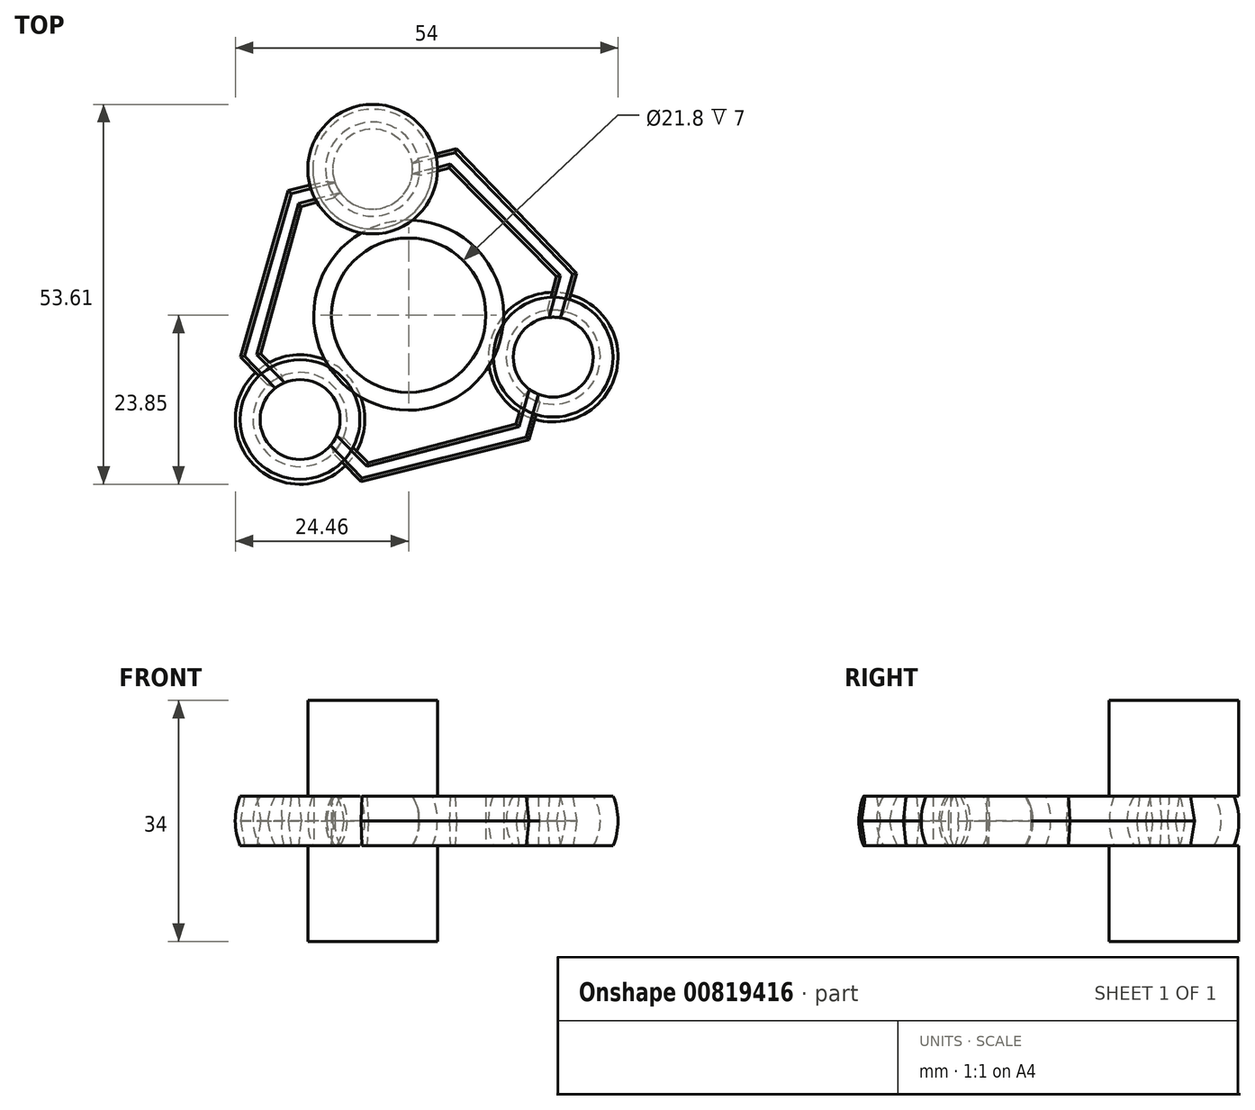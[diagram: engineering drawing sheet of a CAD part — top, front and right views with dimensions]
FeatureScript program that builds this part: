
annotation { "Feature Type Name" : "Feature", "Feature Type Description" : "" }
export const myFeature = defineFeature(function(context is Context, id is Id, definition is map)
    precondition{}
    {
        {
            var Q0;
            Q0=qCreatedBy(makeId("Top.planeOp"),FACE);
            var sketch = newSketch(context, id + "F0", { "sketchPlane" : qUnion([Q0])});
            skCircle(sketch, "E0", {"center": v(0, 0) * mm, "radius": 10.9 * mm});
            skCircle(sketch, "E1", {"center": v(0, 0) * mm, "radius": 13.4 * mm});
            skCircle(sketch, "E2", {"center": v(0, 0) * mm, "radius": 20 * mm, "construction": true});
            skCircle(sketch, "E3", {"center": v(0, 0) * mm, "radius": 18.75 * mm});
            skCircle(sketch, "E4", {"center": v(0, 0) * mm, "radius": 21.25 * mm});
            skSolve(sketch);
        }
        {
            var Q0;
            Q0=makeQuery(id+"F0.imprint","IMPRINT",FACE,{"disambiguationData":[TD([[makeQuery(id+"F0.imprint","IMPRINT",EDGE,{"derivedFrom":sQuery(id+"F0.wireOp",EDGE,"E3")}),-1.0]])]});
            var sketch = newSketch(context, id + "F1", { "sketchPlane" : qUnion([Q0])});
            skCircle(sketch, "E5", {"center": v(-5.08, 20.62) * mm, "radius": 6.64 * mm});
            skCircle(sketch, "E6", {"center": v(-5.08, 20.62) * mm, "radius": 9.14 * mm});
            skSolve(sketch);
        }
        {
            var Q0;
            Q0=makeQuery(id+"F0.imprint","IMPRINT",FACE,{"disambiguationData":[TD([[makeQuery(id+"F0.imprint","IMPRINT",EDGE,{"derivedFrom":sQuery(id+"F0.wireOp",EDGE,"E0")}),1.0]])]});
            var sketch = newSketch(context, id + "F2", { "sketchPlane" : qUnion([Q0])});
            skCircle(sketch, "E7.cCircle", {"center": v(0, 0) * mm, "radius": 21.16 * mm, "construction": true});
            skLineSegment(sketch, "E7.0", {"start": v(-16.97, 17.58) * mm, "end": v(6.74, 23.5) * mm});
            skLineSegment(sketch, "E7.1", {"start": v(6.74, 23.5) * mm, "end": v(23.71, 5.9) * mm});
            skLineSegment(sketch, "E7.2", {"start": v(23.71, 5.9) * mm, "end": v(16.97, -17.58) * mm});
            skLineSegment(sketch, "E7.3", {"start": v(16.97, -17.58) * mm, "end": v(-6.74, -23.5) * mm});
            skLineSegment(sketch, "E7.4", {"start": v(-6.74, -23.5) * mm, "end": v(-23.71, -5.9) * mm});
            skLineSegment(sketch, "E7.5", {"start": v(-23.71, -5.9) * mm, "end": v(-16.97, 17.58) * mm});
            skPoint(sketch, "E7.0.midPoint", {"position": v(-5.12, 20.54) * mm});
            skCircle(sketch, "E8.cCircle", {"center": v(0, 0) * mm, "radius": 18.68 * mm, "construction": true});
            skLineSegment(sketch, "E8.0", {"start": v(-15.15, 15.35) * mm, "end": v(5.72, 20.8) * mm});
            skLineSegment(sketch, "E8.1", {"start": v(5.72, 20.8) * mm, "end": v(20.87, 5.45) * mm});
            skLineSegment(sketch, "E8.2", {"start": v(20.87, 5.45) * mm, "end": v(15.15, -15.35) * mm});
            skLineSegment(sketch, "E8.3", {"start": v(15.15, -15.35) * mm, "end": v(-5.72, -20.8) * mm});
            skLineSegment(sketch, "E8.4", {"start": v(-5.72, -20.8) * mm, "end": v(-20.87, -5.45) * mm});
            skLineSegment(sketch, "E8.5", {"start": v(-20.87, -5.45) * mm, "end": v(-15.15, 15.35) * mm});
            skPoint(sketch, "E8.0.midPoint", {"position": v(-4.72, 18.07) * mm});
            skSolve(sketch);
        }
        {
            var Q0;
            {var subQ0=sQuery(id+"F1.wireOp",EDGE,"E5");var subQ1=makeQuery(id+"F0.imprint","IMPRINT",EDGE,{"derivedFrom":sQuery(id+"F0.wireOp",EDGE,"E4")});var subQ2=makeQuery(id+"F1.imprint","INTERSECT",VERTEX,{"disambiguationData":[OD(0.0)],"derivedFrom":[subQ1,subQ0]});Q0=makeQuery(id+"F1.imprint","IMPRINT",FACE,{"disambiguationData":[TD([[makeQuery(id+"F1.imprint","IMPRINT",EDGE,{"disambiguationData":[TD([[subQ2,1.0]])],"derivedFrom":subQ0}),1.0]])]});}
            var Q1;
            {var subQ0=sQuery(id+"F1.wireOp",EDGE,"E5");var subQ1=makeQuery(id+"F0.imprint","IMPRINT",EDGE,{"derivedFrom":sQuery(id+"F0.wireOp",EDGE,"E4")});var subQ2=makeQuery(id+"F1.imprint","INTERSECT",VERTEX,{"disambiguationData":[OD(0.0)],"derivedFrom":[subQ1,subQ0]});Q1=makeQuery(id+"F1.imprint","IMPRINT",FACE,{"disambiguationData":[TD([[makeQuery(id+"F1.imprint","IMPRINT",EDGE,{"disambiguationData":[TD([[subQ2,-1.0]])],"derivedFrom":subQ0}),1.0]])]});}
            var Q2;
            {var subQ0=sQuery(id+"F1.wireOp",EDGE,"E5");var subQ1=makeQuery(id+"F0.imprint","IMPRINT",EDGE,{"derivedFrom":sQuery(id+"F0.wireOp",EDGE,"E3")});var subQ2=makeQuery(id+"F1.imprint","INTERSECT",VERTEX,{"disambiguationData":[OD(0.0)],"derivedFrom":[subQ1,subQ0]});Q2=makeQuery(id+"F1.imprint","IMPRINT",FACE,{"disambiguationData":[TD([[makeQuery(id+"F1.imprint","IMPRINT",EDGE,{"disambiguationData":[TD([[subQ2,-1.0]])],"derivedFrom":subQ0}),1.0]])]});}
            extrude(context, id + "F3", {"entities" : qUnion([Q0, Q1, Q2]), "depth" : (13.28 / 2) * mm, "offsetDistance" : 25 * mm, "hasSecondDirection" : true, "secondDirectionOppositeDirection" : true, "secondDirectionDepth" : 6.64 * mm});
        }
        {
            var Q0;
            Q0=makeQuery(id+"F3.opExtrude","CAP_EDGE",EDGE,{"disambiguationData":[OSD([sQuery(id+"F1.wireOp",EDGE,"E5")])],"isStart":false});
            var Q1;
            Q1=makeQuery(id+"F3.opExtrude","CAP_EDGE",EDGE,{"disambiguationData":[OSD([sQuery(id+"F1.wireOp",EDGE,"E5")])],"isStart":true});
            fillet(context, id + "F4", {"entities" : qUnion([Q0, Q1]), "radius" : 6.64 * mm, "tangentPropagation" : true, "allowEdgeOverflow" : false});
        }
        {
            var Q0;
            {var subQ0=sQuery(id+"F1.wireOp",EDGE,"E5");var subQ1=makeQuery(id+"F0.imprint","IMPRINT",EDGE,{"derivedFrom":sQuery(id+"F0.wireOp",EDGE,"E4")});var subQ2=makeQuery(id+"F1.imprint","INTERSECT",VERTEX,{"disambiguationData":[OD(0.0)],"derivedFrom":[subQ1,subQ0]});Q0=makeQuery(id+"F1.imprint","IMPRINT",FACE,{"disambiguationData":[TD([[makeQuery(id+"F1.imprint","IMPRINT",EDGE,{"disambiguationData":[TD([[subQ2,1.0]])],"derivedFrom":subQ0}),-1.0]])]});}
            var Q1;
            {var subQ0=sQuery(id+"F1.wireOp",EDGE,"E5");var subQ1=makeQuery(id+"F0.imprint","IMPRINT",EDGE,{"derivedFrom":sQuery(id+"F0.wireOp",EDGE,"E4")});var subQ2=makeQuery(id+"F1.imprint","INTERSECT",VERTEX,{"disambiguationData":[OD(0.0)],"derivedFrom":[subQ1,subQ0]});Q1=makeQuery(id+"F1.imprint","IMPRINT",FACE,{"disambiguationData":[TD([[makeQuery(id+"F1.imprint","IMPRINT",EDGE,{"disambiguationData":[TD([[subQ2,1.0]])],"derivedFrom":subQ0}),1.0]])]});}
            var Q2;
            {var subQ0=sQuery(id+"F1.wireOp",EDGE,"E5");var subQ1=makeQuery(id+"F0.imprint","IMPRINT",EDGE,{"derivedFrom":sQuery(id+"F0.wireOp",EDGE,"E4")});var subQ2=makeQuery(id+"F1.imprint","INTERSECT",VERTEX,{"disambiguationData":[OD(0.0)],"derivedFrom":[subQ1,subQ0]});Q2=makeQuery(id+"F1.imprint","IMPRINT",FACE,{"disambiguationData":[TD([[makeQuery(id+"F1.imprint","IMPRINT",EDGE,{"disambiguationData":[TD([[subQ2,-1.0]])],"derivedFrom":subQ0}),1.0]])]});}
            var Q3;
            {var subQ0=sQuery(id+"F1.wireOp",EDGE,"E5");var subQ1=makeQuery(id+"F0.imprint","IMPRINT",EDGE,{"derivedFrom":sQuery(id+"F0.wireOp",EDGE,"E3")});var subQ2=makeQuery(id+"F1.imprint","INTERSECT",VERTEX,{"disambiguationData":[OD(0.0)],"derivedFrom":[subQ1,subQ0]});Q3=makeQuery(id+"F1.imprint","IMPRINT",FACE,{"disambiguationData":[TD([[makeQuery(id+"F1.imprint","IMPRINT",EDGE,{"disambiguationData":[TD([[subQ2,-1.0]])],"derivedFrom":subQ0}),1.0]])]});}
            var Q4;
            {var subQ0=sQuery(id+"F1.wireOp",EDGE,"E5");var subQ1=makeQuery(id+"F0.imprint","IMPRINT",EDGE,{"derivedFrom":sQuery(id+"F0.wireOp",EDGE,"E3")});var subQ2=makeQuery(id+"F1.imprint","INTERSECT",VERTEX,{"disambiguationData":[OD(0.0)],"derivedFrom":[subQ1,subQ0]});Q4=makeQuery(id+"F1.imprint","IMPRINT",FACE,{"disambiguationData":[TD([[makeQuery(id+"F1.imprint","IMPRINT",EDGE,{"disambiguationData":[TD([[subQ2,-1.0]])],"derivedFrom":subQ0}),-1.0]])]});}
            var Q5;
            {var subQ0=sQuery(id+"F1.wireOp",EDGE,"E5");var subQ1=makeQuery(id+"F0.imprint","IMPRINT",EDGE,{"derivedFrom":sQuery(id+"F0.wireOp",EDGE,"E4")});var subQ2=makeQuery(id+"F1.imprint","INTERSECT",VERTEX,{"disambiguationData":[OD(1.0)],"derivedFrom":[subQ1,subQ0]});Q5=makeQuery(id+"F1.imprint","IMPRINT",FACE,{"disambiguationData":[TD([[makeQuery(id+"F1.imprint","IMPRINT",EDGE,{"disambiguationData":[TD([[subQ2,1.0]])],"derivedFrom":subQ0}),-1.0]])]});}
            var Q6;
            {var subQ0=sQuery(id+"F1.wireOp",EDGE,"E5");var subQ1=makeQuery(id+"F0.imprint","IMPRINT",EDGE,{"derivedFrom":sQuery(id+"F0.wireOp",EDGE,"E4")});var subQ2=makeQuery(id+"F1.imprint","INTERSECT",VERTEX,{"disambiguationData":[OD(0.0)],"derivedFrom":[subQ1,subQ0]});Q6=makeQuery(id+"F1.imprint","IMPRINT",FACE,{"disambiguationData":[TD([[makeQuery(id+"F1.imprint","IMPRINT",EDGE,{"disambiguationData":[TD([[subQ2,-1.0]])],"derivedFrom":subQ0}),-1.0]])]});}
            extrude(context, id + "F5", {"entities" : qUnion([Q0, Q1, Q2, Q3, Q4, Q5, Q6]), "depth" : 17 * mm, "offsetDistance" : 25 * mm, "hasSecondDirection" : true, "secondDirectionOppositeDirection" : false, "secondDirectionDepth" : 3.5 * mm});
        }
        {
            var Q0;
            Q0=makeQuery(id+"F5.opExtrude","SWEPT_BODY",BODY,{"disambiguationData":[OSD([sQuery(id+"F1.wireOp",EDGE,"E6")])]});
            var Q1;
            {var subQ0=sQuery(id+"F1.wireOp",EDGE,"E5");var subQ1=makeQuery(id+"F0.imprint","IMPRINT",EDGE,{"derivedFrom":sQuery(id+"F0.wireOp",EDGE,"E4")});var subQ2=makeQuery(id+"F1.imprint","INTERSECT",VERTEX,{"disambiguationData":[OD(0.0)],"derivedFrom":[subQ1,subQ0]});Q1=makeQuery(id+"F1.imprint","IMPRINT",FACE,{"disambiguationData":[TD([[makeQuery(id+"F1.imprint","IMPRINT",EDGE,{"disambiguationData":[TD([[subQ2,1.0]])],"derivedFrom":subQ0}),1.0]])]});}
            mirror(context, id + "F6", {"entities" : qUnion([Q0]), "mirrorPlane" : qUnion([Q1])});
        }
        {
            var Q0;
            {var subQ0=sQuery(id+"F1.wireOp",EDGE,"E5");var subQ1=makeQuery(id+"F0.imprint","IMPRINT",EDGE,{"derivedFrom":sQuery(id+"F0.wireOp",EDGE,"E4")});var subQ2=makeQuery(id+"F1.imprint","INTERSECT",VERTEX,{"disambiguationData":[OD(0.0)],"derivedFrom":[subQ1,subQ0]});Q0=makeQuery(id+"F1.imprint","IMPRINT",FACE,{"disambiguationData":[TD([[makeQuery(id+"F1.imprint","IMPRINT",EDGE,{"disambiguationData":[TD([[subQ2,1.0]])],"derivedFrom":subQ0}),1.0]])]});}
            var Q1;
            {var subQ0=sQuery(id+"F1.wireOp",EDGE,"E5");var subQ1=makeQuery(id+"F0.imprint","IMPRINT",EDGE,{"derivedFrom":sQuery(id+"F0.wireOp",EDGE,"E4")});var subQ2=makeQuery(id+"F1.imprint","INTERSECT",VERTEX,{"disambiguationData":[OD(0.0)],"derivedFrom":[subQ1,subQ0]});Q1=makeQuery(id+"F1.imprint","IMPRINT",FACE,{"disambiguationData":[TD([[makeQuery(id+"F1.imprint","IMPRINT",EDGE,{"disambiguationData":[TD([[subQ2,-1.0]])],"derivedFrom":subQ0}),1.0]])]});}
            var Q2;
            {var subQ0=sQuery(id+"F1.wireOp",EDGE,"E5");var subQ1=makeQuery(id+"F0.imprint","IMPRINT",EDGE,{"derivedFrom":sQuery(id+"F0.wireOp",EDGE,"E3")});var subQ2=makeQuery(id+"F1.imprint","INTERSECT",VERTEX,{"disambiguationData":[OD(0.0)],"derivedFrom":[subQ1,subQ0]});Q2=makeQuery(id+"F1.imprint","IMPRINT",FACE,{"disambiguationData":[TD([[makeQuery(id+"F1.imprint","IMPRINT",EDGE,{"disambiguationData":[TD([[subQ2,-1.0]])],"derivedFrom":subQ0}),1.0]])]});}
            var Q3;
            {var subQ0=sQuery(id+"F1.wireOp",EDGE,"E5");var subQ1=makeQuery(id+"F0.imprint","IMPRINT",EDGE,{"derivedFrom":sQuery(id+"F0.wireOp",EDGE,"E3")});var subQ2=makeQuery(id+"F1.imprint","INTERSECT",VERTEX,{"disambiguationData":[OD(0.0)],"derivedFrom":[subQ1,subQ0]});Q3=makeQuery(id+"F1.imprint","IMPRINT",FACE,{"disambiguationData":[TD([[makeQuery(id+"F1.imprint","IMPRINT",EDGE,{"disambiguationData":[TD([[subQ2,-1.0]])],"derivedFrom":subQ0}),-1.0]])]});}
            var Q4;
            {var subQ0=sQuery(id+"F1.wireOp",EDGE,"E5");var subQ1=makeQuery(id+"F0.imprint","IMPRINT",EDGE,{"derivedFrom":sQuery(id+"F0.wireOp",EDGE,"E4")});var subQ2=makeQuery(id+"F1.imprint","INTERSECT",VERTEX,{"disambiguationData":[OD(1.0)],"derivedFrom":[subQ1,subQ0]});Q4=makeQuery(id+"F1.imprint","IMPRINT",FACE,{"disambiguationData":[TD([[makeQuery(id+"F1.imprint","IMPRINT",EDGE,{"disambiguationData":[TD([[subQ2,1.0]])],"derivedFrom":subQ0}),-1.0]])]});}
            var Q5;
            {var subQ0=sQuery(id+"F1.wireOp",EDGE,"E5");var subQ1=makeQuery(id+"F0.imprint","IMPRINT",EDGE,{"derivedFrom":sQuery(id+"F0.wireOp",EDGE,"E4")});var subQ2=makeQuery(id+"F1.imprint","INTERSECT",VERTEX,{"disambiguationData":[OD(0.0)],"derivedFrom":[subQ1,subQ0]});Q5=makeQuery(id+"F1.imprint","IMPRINT",FACE,{"disambiguationData":[TD([[makeQuery(id+"F1.imprint","IMPRINT",EDGE,{"disambiguationData":[TD([[subQ2,1.0]])],"derivedFrom":subQ0}),-1.0]])]});}
            var Q6;
            {var subQ0=sQuery(id+"F1.wireOp",EDGE,"E5");var subQ1=makeQuery(id+"F0.imprint","IMPRINT",EDGE,{"derivedFrom":sQuery(id+"F0.wireOp",EDGE,"E4")});var subQ2=makeQuery(id+"F1.imprint","INTERSECT",VERTEX,{"disambiguationData":[OD(0.0)],"derivedFrom":[subQ1,subQ0]});Q6=makeQuery(id+"F1.imprint","IMPRINT",FACE,{"disambiguationData":[TD([[makeQuery(id+"F1.imprint","IMPRINT",EDGE,{"disambiguationData":[TD([[subQ2,-1.0]])],"derivedFrom":subQ0}),-1.0]])]});}
            extrude(context, id + "F7", {"entities" : qUnion([Q0, Q1, Q2, Q3, Q4, Q5, Q6]), "depth" : (18.28 / 2) * mm, "offsetDistance" : 25 * mm, "hasSecondDirection" : true, "secondDirectionOppositeDirection" : true, "secondDirectionDepth" : 9.14 * mm});
        }
        {
            var Q0;
            Q0=makeQuery(id+"F7.opExtrude","CAP_EDGE",EDGE,{"disambiguationData":[OSD([sQuery(id+"F1.wireOp",EDGE,"E6")])],"isStart":false});
            var Q1;
            Q1=makeQuery(id+"F7.opExtrude","CAP_EDGE",EDGE,{"disambiguationData":[OSD([sQuery(id+"F1.wireOp",EDGE,"E6")])],"isStart":true});
            fillet(context, id + "F8", {"entities" : qUnion([Q0, Q1]), "radius" : (18.28 / 2) * mm, "tangentPropagation" : true, "allowEdgeOverflow" : false});
        }
        {
            var Q0;
            Q0=makeQuery(id+"F3.opExtrude","SWEPT_BODY",BODY,{"disambiguationData":[OSD([sQuery(id+"F1.wireOp",EDGE,"E5")])]});
            var Q1;
            Q1=makeQuery(id+"F5.opExtrude","SWEPT_BODY",BODY,{"disambiguationData":[OSD([sQuery(id+"F1.wireOp",EDGE,"E6")])]});
            var Q2;
            Q2=makeQuery(id+"F6.opPattern","COPY",BODY,{"derivedFrom":makeQuery(id+"F5.opExtrude","SWEPT_BODY",BODY,{"disambiguationData":[OSD([sQuery(id+"F1.wireOp",EDGE,"E6")])]}),"instanceName":"1"});
            var Q3;
            Q3=makeQuery(id+"F7.opExtrude","SWEPT_BODY",BODY,{"disambiguationData":[OSD([sQuery(id+"F1.wireOp",EDGE,"E6")])]});
            booleanBodies(context, id + "F9", {"operationType" : BooleanOperationType.SUBTRACTION, "tools" : qUnion([Q0, Q1, Q2]), "targets" : qUnion([Q3]), "keepTools" : true});
        }
        {
            var Q0;
            Q0=makeQuery(id+"F7.opExtrude","SWEPT_BODY",BODY,{"disambiguationData":[OSD([sQuery(id+"F1.wireOp",EDGE,"E6")])]});
            var Q1;
            Q1=sQuery(id+"F0.wireOp",EDGE,"E2");
            circularPattern(context, id + "F10", {"entities" : qUnion([Q0]), "axis" : qUnion([Q1]), "angle" : 360 * degree, "instanceCount" : 3, "equalSpace" : true});
        }
        {
            var Q0;
            Q0=makeQuery(id+"F2.imprint","IMPRINT",FACE,{"disambiguationData":[TD([[makeQuery(id+"F2.imprint","IMPRINT",EDGE,{"derivedFrom":sQuery(id+"F2.wireOp",EDGE,"E7.0")}),-1.0]])]});
            extrude(context, id + "F11", {"entities" : qUnion([Q0]), "depth" : 3.5 * mm, "offsetDistance" : 25 * mm, "hasDraft" : true, "draftAngle" : 8 * degree, "draftPullDirection" : true, "hasSecondDirection" : true, "secondDirectionOppositeDirection" : true, "secondDirectionDepth" : 3.5 * mm, "hasSecondDirectionDraft" : true, "secondDirectionDraftAngle" : 7.9 * degree, "secondDirectionDraftPullDirection" : true});
        }
        {
            var Q0;
            Q0=makeQuery(id+"F0.imprint","IMPRINT",FACE,{"disambiguationData":[TD([[makeQuery(id+"F0.imprint","IMPRINT",EDGE,{"derivedFrom":sQuery(id+"F0.wireOp",EDGE,"E0")}),-1.0]])]});
            extrude(context, id + "F12", {"entities" : qUnion([Q0]), "depth" : 3.5 * mm, "offsetDistance" : 25 * mm, "hasSecondDirection" : true, "secondDirectionOppositeDirection" : true, "secondDirectionDepth" : 3.5 * mm});
        }
        {
            var Q0;
            Q0=makeQuery(id+"F3.opExtrude","SWEPT_BODY",BODY,{"disambiguationData":[OSD([sQuery(id+"F1.wireOp",EDGE,"E5")])]});
            var Q1;
            Q1=makeQuery(id+"F12.opExtrude","CAP_EDGE",EDGE,{"disambiguationData":[OSD([sQuery(id+"F0.wireOp",EDGE,"E0")])],"isStart":false});
            circularPattern(context, id + "F13", {"entities" : qUnion([Q0]), "axis" : qUnion([Q1]), "angle" : 360 * degree, "instanceCount" : 3, "equalSpace" : true});
        }
        {
            var Q0;
            Q0=makeQuery(id+"F13.opPattern","COPY",BODY,{"derivedFrom":makeQuery(id+"F3.opExtrude","SWEPT_BODY",BODY,{"disambiguationData":[OSD([sQuery(id+"F1.wireOp",EDGE,"E5")])]}),"instanceName":"2"});
            var Q1;
            Q1=makeQuery(id+"F13.opPattern","COPY",BODY,{"derivedFrom":makeQuery(id+"F3.opExtrude","SWEPT_BODY",BODY,{"disambiguationData":[OSD([sQuery(id+"F1.wireOp",EDGE,"E5")])]}),"instanceName":"1"});
            var Q2;
            Q2=makeQuery(id+"F3.opExtrude","SWEPT_BODY",BODY,{"disambiguationData":[OSD([sQuery(id+"F1.wireOp",EDGE,"E5")])]});
            var Q3;
            Q3=makeQuery(id+"F11.*.split.splitOp","SPLIT",BODY,{"derivedFrom":makeQuery(id+"F11.opExtrude","SWEPT_BODY",BODY,{"disambiguationData":[OSD([sQuery(id+"F2.wireOp",EDGE,"E7.0"),sQuery(id+"F2.wireOp",EDGE,"E7.1"),sQuery(id+"F2.wireOp",EDGE,"E7.2"),sQuery(id+"F2.wireOp",EDGE,"E7.3"),sQuery(id+"F2.wireOp",EDGE,"E7.4"),sQuery(id+"F2.wireOp",EDGE,"E7.5"),sQuery(id+"F2.wireOp",EDGE,"E8.0"),sQuery(id+"F2.wireOp",EDGE,"E8.1"),sQuery(id+"F2.wireOp",EDGE,"E8.2"),sQuery(id+"F2.wireOp",EDGE,"E8.3"),sQuery(id+"F2.wireOp",EDGE,"E8.4"),sQuery(id+"F2.wireOp",EDGE,"E8.5")])]})});
            booleanBodies(context, id + "F14", {"operationType" : BooleanOperationType.SUBTRACTION, "tools" : qUnion([Q0, Q1, Q2]), "targets" : qUnion([Q3])});
        }
    });
